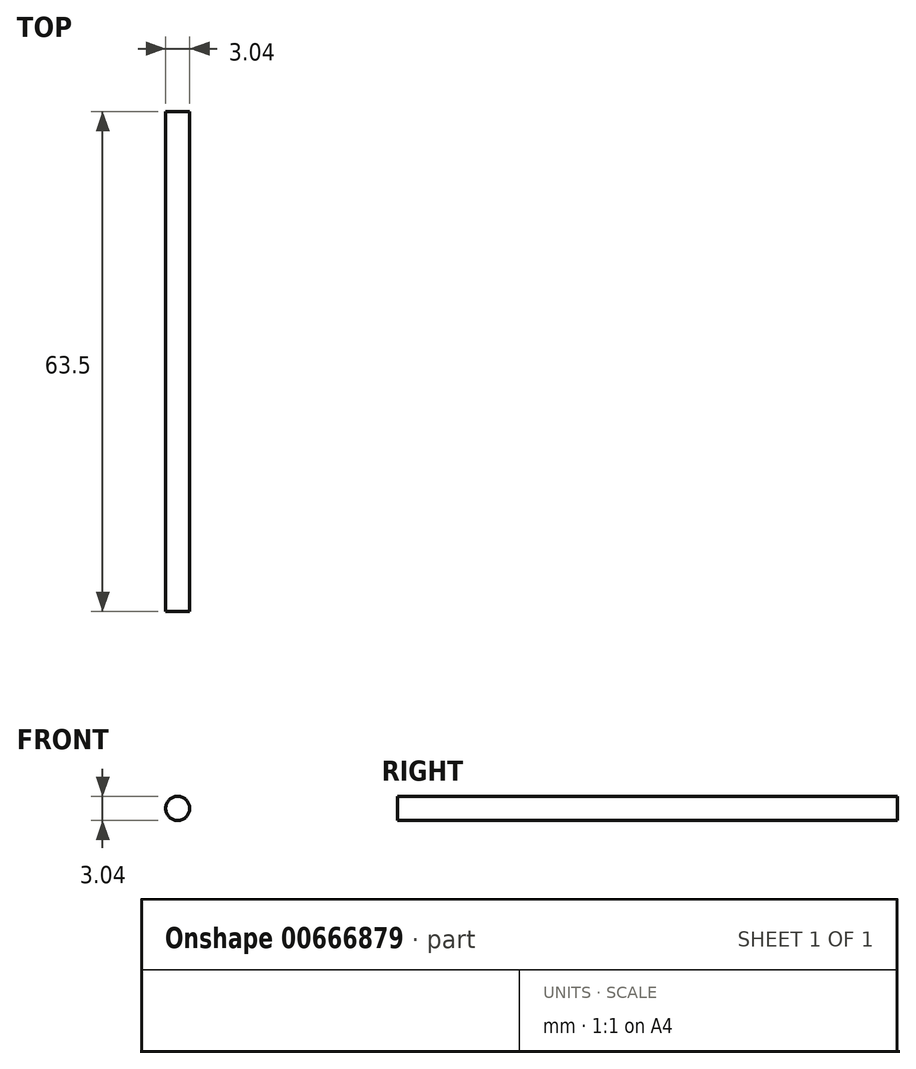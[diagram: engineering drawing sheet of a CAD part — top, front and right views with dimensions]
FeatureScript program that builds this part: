
annotation { "Feature Type Name" : "Feature", "Feature Type Description" : "" }
export const myFeature = defineFeature(function(context is Context, id is Id, definition is map)
    precondition{}
    {
        {
            var Q0;
            Q0=qCreatedBy(makeId("Front.planeOp"),FACE);
            var sketch = newSketch(context, id + "F0", { "sketchPlane" : qUnion([Q0])});
            skCircle(sketch, "E0", {"center": v(0, 0) * mm, "radius": 1.52 * mm});
            skSolve(sketch);
        }
        {
            var Q0;
            Q0=makeQuery(id+"F0.imprint","IMPRINT",FACE,{"disambiguationData":[TD([[makeQuery(id+"F0.imprint","IMPRINT",EDGE,{"derivedFrom":sQuery(id+"F0.wireOp",EDGE,"E0")}),1.0]])]});
            extrude(context, id + "F1", {"entities" : qUnion([Q0]), "depth" : 63.5 * mm, "offsetDistance" : 25.4 * mm});
        }
    });
